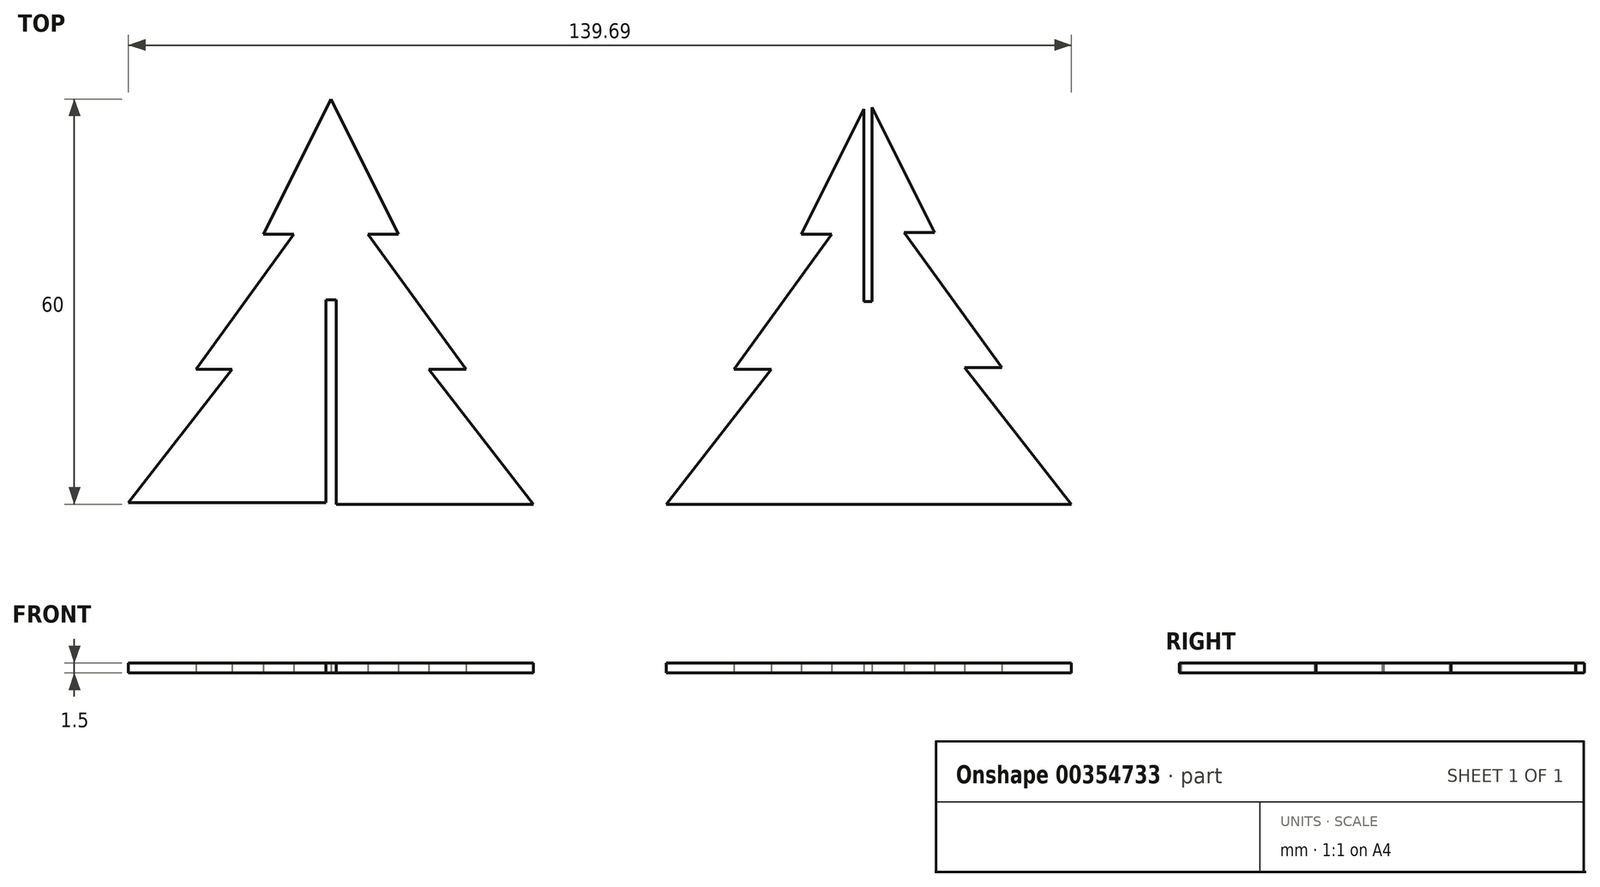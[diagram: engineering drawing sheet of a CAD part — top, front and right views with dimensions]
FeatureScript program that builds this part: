
annotation { "Feature Type Name" : "Feature", "Feature Type Description" : "" }
export const myFeature = defineFeature(function(context is Context, id is Id, definition is map)
    precondition{}
    {
        {
            var Q0;
            Q0=qCreatedBy(makeId("Top.planeOp"),FACE);
            var sketch = newSketch(context, id + "F0", { "sketchPlane" : qUnion([Q0])});
            skLineSegment(sketch, "E0", {"start": v(0, 0) * mm, "end": v(30, 0) * mm});
            skLineSegment(sketch, "E1", {"start": v(30, 0) * mm, "end": v(14.2, 20.25) * mm});
            skLineSegment(sketch, "E2", {"start": v(14.2, 20.25) * mm, "end": v(19.7, 20.25) * mm});
            skLineSegment(sketch, "E3", {"start": v(19.7, 20.25) * mm, "end": v(5.2, 40.25) * mm});
            skLineSegment(sketch, "E4", {"start": v(5.2, 40.25) * mm, "end": v(9.7, 40.25) * mm});
            skLineSegment(sketch, "E5.MirrorCS", {"start": v(-5.5, 40) * mm, "end": v(-10, 40) * mm});
            skLineSegment(sketch, "E6.MirrorCS", {"start": v(-20, 20) * mm, "end": v(-5.5, 40) * mm});
            skLineSegment(sketch, "E7.MirrorCS", {"start": v(-14.5, 20) * mm, "end": v(-20, 20) * mm});
            skLineSegment(sketch, "E8.MirrorCS", {"start": v(-30, 0) * mm, "end": v(-14.5, 20) * mm});
            skLineSegment(sketch, "E9.MirrorCS", {"start": v(0, 0) * mm, "end": v(-30, 0) * mm});
            skLineSegment(sketch, "E10.MirrorCS", {"start": v(-79.69, 60) * mm, "end": v(-69.69, 40) * mm});
            skLineSegment(sketch, "E11.MirrorCS", {"start": v(-79.69, 60) * mm, "end": v(-89.69, 40) * mm});
            skLineSegment(sketch, "E12.MirrorCS", {"start": v(-85.19, 40) * mm, "end": v(-89.69, 40) * mm});
            skLineSegment(sketch, "E13.MirrorCS", {"start": v(-74.19, 40) * mm, "end": v(-69.69, 40) * mm});
            skLineSegment(sketch, "E14.MirrorCS", {"start": v(-59.69, 20) * mm, "end": v(-74.19, 40) * mm});
            skLineSegment(sketch, "E15.MirrorCS", {"start": v(-99.69, 20) * mm, "end": v(-85.19, 40) * mm});
            skLineSegment(sketch, "E16.MirrorCS", {"start": v(-94.19, 20) * mm, "end": v(-99.69, 20) * mm});
            skLineSegment(sketch, "E17.MirrorCS", {"start": v(-109.69, 0.25) * mm, "end": v(-94.19, 20.25) * mm});
            skLineSegment(sketch, "E18.MirrorCS", {"start": v(-49.69, 0) * mm, "end": v(-65.19, 20) * mm});
            skLineSegment(sketch, "E19.MirrorCS", {"start": v(-65.19, 20) * mm, "end": v(-59.69, 20) * mm});
            skLineSegment(sketch, "E20", {"start": v(0, 30) * mm, "end": v(0.45, 30) * mm, "construction": true});
            skLineSegment(sketch, "E21", {"start": v(0, 30) * mm, "end": v(-0.75, 30) * mm, "construction": true});
            skLineSegment(sketch, "E22", {"start": v(-0.75, 30) * mm, "end": v(-0.75, 58.5) * mm});
            skLineSegment(sketch, "E23", {"start": v(0.45, 30) * mm, "end": v(0.45, 58.75) * mm});
            skLineSegment(sketch, "E24", {"start": v(-0.75, 30) * mm, "end": v(0.45, 30) * mm});
            skLineSegment(sketch, "E25", {"start": v(-0.75, 58.5) * mm, "end": v(-10, 40) * mm});
            skLineSegment(sketch, "E26", {"start": v(0.45, 58.75) * mm, "end": v(9.7, 40.25) * mm});
            skLineSegment(sketch, "E27", {"start": v(-79.69, 30.25) * mm, "end": v(-78.94, 30.25) * mm, "construction": true});
            skLineSegment(sketch, "E28", {"start": v(-79.69, 30.25) * mm, "end": v(-80.44, 30.25) * mm, "construction": true});
            skLineSegment(sketch, "E29", {"start": v(-80.44, 30.25) * mm, "end": v(-80.44, 0.25) * mm});
            skLineSegment(sketch, "E30", {"start": v(-78.94, 30.25) * mm, "end": v(-78.94, 0) * mm});
            skLineSegment(sketch, "E31", {"start": v(-80.44, 30.25) * mm, "end": v(-78.94, 30.25) * mm});
            skLineSegment(sketch, "E32", {"start": v(-109.69, 0.25) * mm, "end": v(-80.44, 0.25) * mm});
            skLineSegment(sketch, "E33", {"start": v(-78.94, 0) * mm, "end": v(-49.69, 0) * mm});
            skSolve(sketch);
        }
        {
            var Q0;
            Q0=makeQuery(id+"F0.imprint","IMPRINT",FACE,{"disambiguationData":[TD([[makeQuery(id+"F0.imprint","IMPRINT",EDGE,{"derivedFrom":sQuery(id+"F0.wireOp",EDGE,"E10.MirrorCS")}),-1.0]])]});
            var Q1;
            Q1=makeQuery(id+"F0.imprint","IMPRINT",FACE,{"disambiguationData":[TD([[makeQuery(id+"F0.imprint","IMPRINT",EDGE,{"derivedFrom":sQuery(id+"F0.wireOp",EDGE,"E0")}),1.0]])]});
            extrude(context, id + "F1", {"entities" : qUnion([Q0, Q1]), "depth" : 1.5 * mm});
        }
    });
